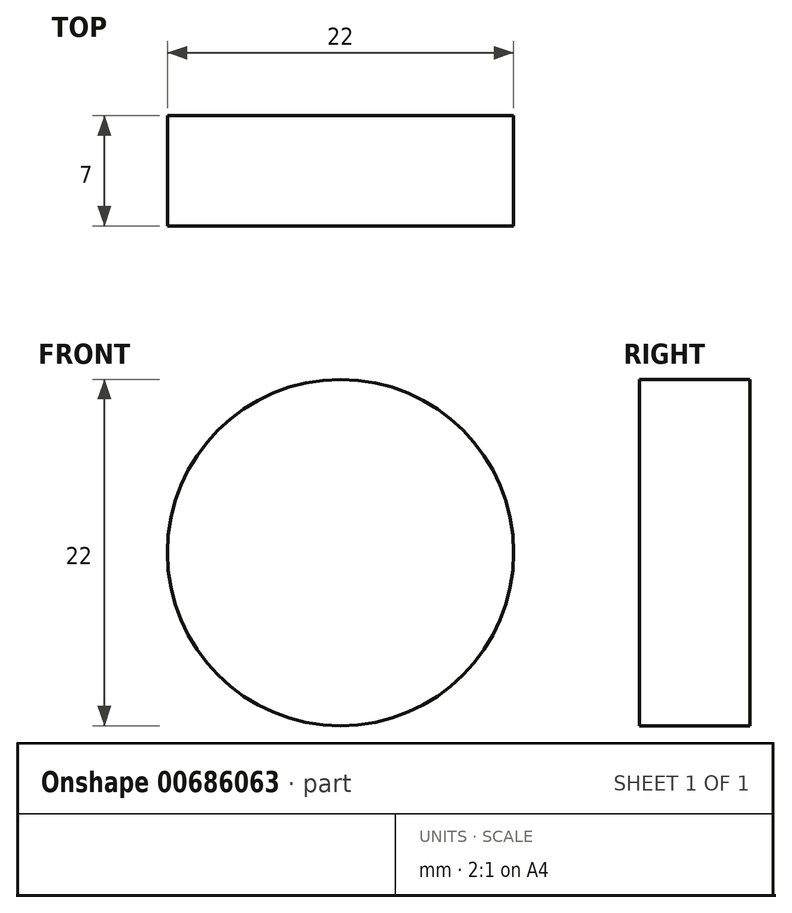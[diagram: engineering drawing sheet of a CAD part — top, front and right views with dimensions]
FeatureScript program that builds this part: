
annotation { "Feature Type Name" : "Feature", "Feature Type Description" : "" }
export const myFeature = defineFeature(function(context is Context, id is Id, definition is map)
    precondition{}
    {
        {
            var Q0;
            Q0=qCreatedBy(makeId("Front.planeOp"),FACE);
            var sketch = newSketch(context, id + "F0", { "sketchPlane" : qUnion([Q0])});
            skCircle(sketch, "E0", {"center": v(0, 0) * mm, "radius": 11 * mm});
            skSolve(sketch);
        }
        {
            var Q0;
            Q0=makeQuery(id+"F0.imprint","IMPRINT",FACE,{"disambiguationData":[TD([[makeQuery(id+"F0.imprint","IMPRINT",EDGE,{"derivedFrom":sQuery(id+"F0.wireOp",EDGE,"E0")}),1.0]])]});
            extrude(context, id + "F1", {"entities" : qUnion([Q0]), "depth" : 7 * mm, "offsetDistance" : 25 * mm});
        }
    });
